# Revit family: AD-S12 - M10 Eye Bolts
name_source: partatom
category: Communication Devices
revit_build: Autodesk Revit Architecture 2012 (Build: 20110309_2315(x64)
units: mm (PartAtom-declared; Revit-internal decimal feet)

## types (1)
- AD-S12 - M10 Eye Bolts
    Coverage Horizontal = 75.00°
    Coverage Vertical = 75.00°
    Description = 12" 2-Way Surface Mount Loudspeaker
    Enclosure Finish = Black Finish
    Grille Finish = Black Grille
    Impedance = 8
    Manufacturer = QSC Audio Products, LLC
    Manufacturer URL = www.qscaudio.com
    Mid Depth = 310.5 mm
    Model = AD-S12
    Power Handling = 300
    Product Documentation Link = TBA
    Product Page URL = TBA
    Regulatory Compliance = RoHS
    Rotation Axis Distance = 3351.0 mm
    SPL Max = 126
    Sensitivity = 92
    URL = TBA
    Weight Dimensional (kg) = 21
    Weight Dimensional (lb) = 46.3
    Weight Product (kg) = 16
    Weight Product (lb) = 35
    Width = 354.0 mm

## geometry (parser evidence)
native form markers: Blend x2, Sweep x3
no freeform markers — native parametric forms only
